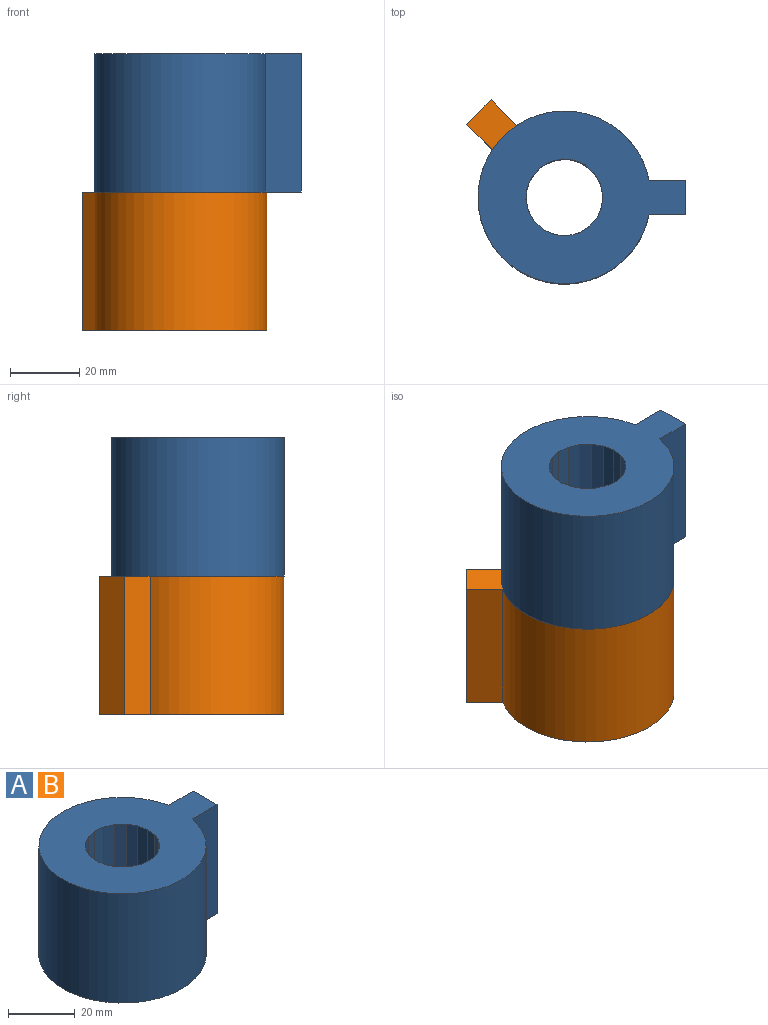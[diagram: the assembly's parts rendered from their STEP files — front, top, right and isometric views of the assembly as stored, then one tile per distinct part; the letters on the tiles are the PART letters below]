
ASSEMBLY  parts=2 mates=1
PART A: 26 faces, bbox 60x50x40 mm
  f0: plane 60x50mm, normal (0,0,1), area 1681.9mm2, adj f2,f3,f4,f5,f6,f7,f8,f9
  f1: plane 60x50mm, normal (0,0,-1), area 1681.9mm2, adj f2,f3,f4,f5,f6,f7,f8,f9
  f2: plane 40x10mm, normal (1,0,0), area 400mm2, adj f0,f1,f3,f5
  f3: plane 40x10.51mm, normal (0,1,0), area 420.2mm2, adj f0,f1,f2,f4
  f4: cylinder r=25mm len=50mm, axis (0,0,-1), area 5880.5mm2, adj f0,f1,f3,f5
  f5: plane 40x10.51mm, normal (0,-1,0), area 420.2mm2, adj f0,f1,f2,f4
  f6: plane 40x2.6mm, normal (0.67,0.75,0), area 139.4mm2, adj f0,f1,f7,f25
  f7: plane 40x3.19mm, normal (0.4,0.92,0), area 139.4mm2, adj f0,f1,f6,f8
  f8: plane 40x3.47mm, normal (0.1,0.99,0), area 139.4mm2, adj f0,f1,f7,f9
  f9: plane 40x3.41mm, normal (-0.21,0.98,0), area 139.4mm2, adj f0,f1,f8,f10
  f10: plane 40x3.01mm, normal (-0.5,0.86,0), area 139.4mm2, adj f0,f1,f9,f11
  f11: plane 40x2.6mm, normal (-0.75,0.67,0), area 139.4mm2, adj f0,f1,f10,f12
  f12: plane 40x3.19mm, normal (-0.92,0.4,0), area 139.4mm2, adj f0,f1,f11,f13
  f13: plane 40x3.47mm, normal (-0.99,0.1,0), area 139.4mm2, adj f0,f1,f12,f14
  f14: plane 40x3.41mm, normal (-0.98,-0.21,0), area 139.4mm2, adj f0,f1,f13,f15
  f15: plane 40x3.01mm, normal (-0.86,-0.5,0), area 139.4mm2, adj f0,f1,f14,f16
  f16: plane 40x2.6mm, normal (-0.67,-0.75,0), area 139.4mm2, adj f0,f1,f15,f17
  f17: plane 40x3.19mm, normal (-0.4,-0.92,0), area 139.4mm2, adj f0,f1,f16,f18
  f18: plane 40x3.47mm, normal (-0.1,-0.99,0), area 139.4mm2, adj f0,f1,f17,f19
  f19: plane 40x3.41mm, normal (0.21,-0.98,0), area 139.4mm2, adj f0,f1,f18,f20
  f20: plane 40x3.01mm, normal (0.5,-0.86,0), area 139.4mm2, adj f0,f1,f19,f21
  f21: plane 40x2.6mm, normal (0.75,-0.67,0), area 139.4mm2, adj f0,f1,f20,f22
  f22: plane 40x3.19mm, normal (0.92,-0.4,0), area 139.4mm2, adj f0,f1,f21,f23
  f23: plane 40x3.47mm, normal (0.99,-0.1,0), area 139.4mm2, adj f0,f1,f22,f24
  f24: plane 40x3.41mm, normal (0.98,0.21,0), area 139.4mm2, adj f0,f1,f23,f25
  f25: plane 40x3.01mm, normal (0.86,0.5,0), area 139.4mm2, adj f0,f1,f6,f24
PART B: same geometry as A
PLACE A t=(8.43,28.36,-5.01)mm
PLACE B rot(axis=(0,0,1),135deg) t=(8.43,28.36,-45.01)mm
MATE revolute B.f4 <-> A.f4  axis (0,0,1) through (8.43,28.36,-5.01)mm
